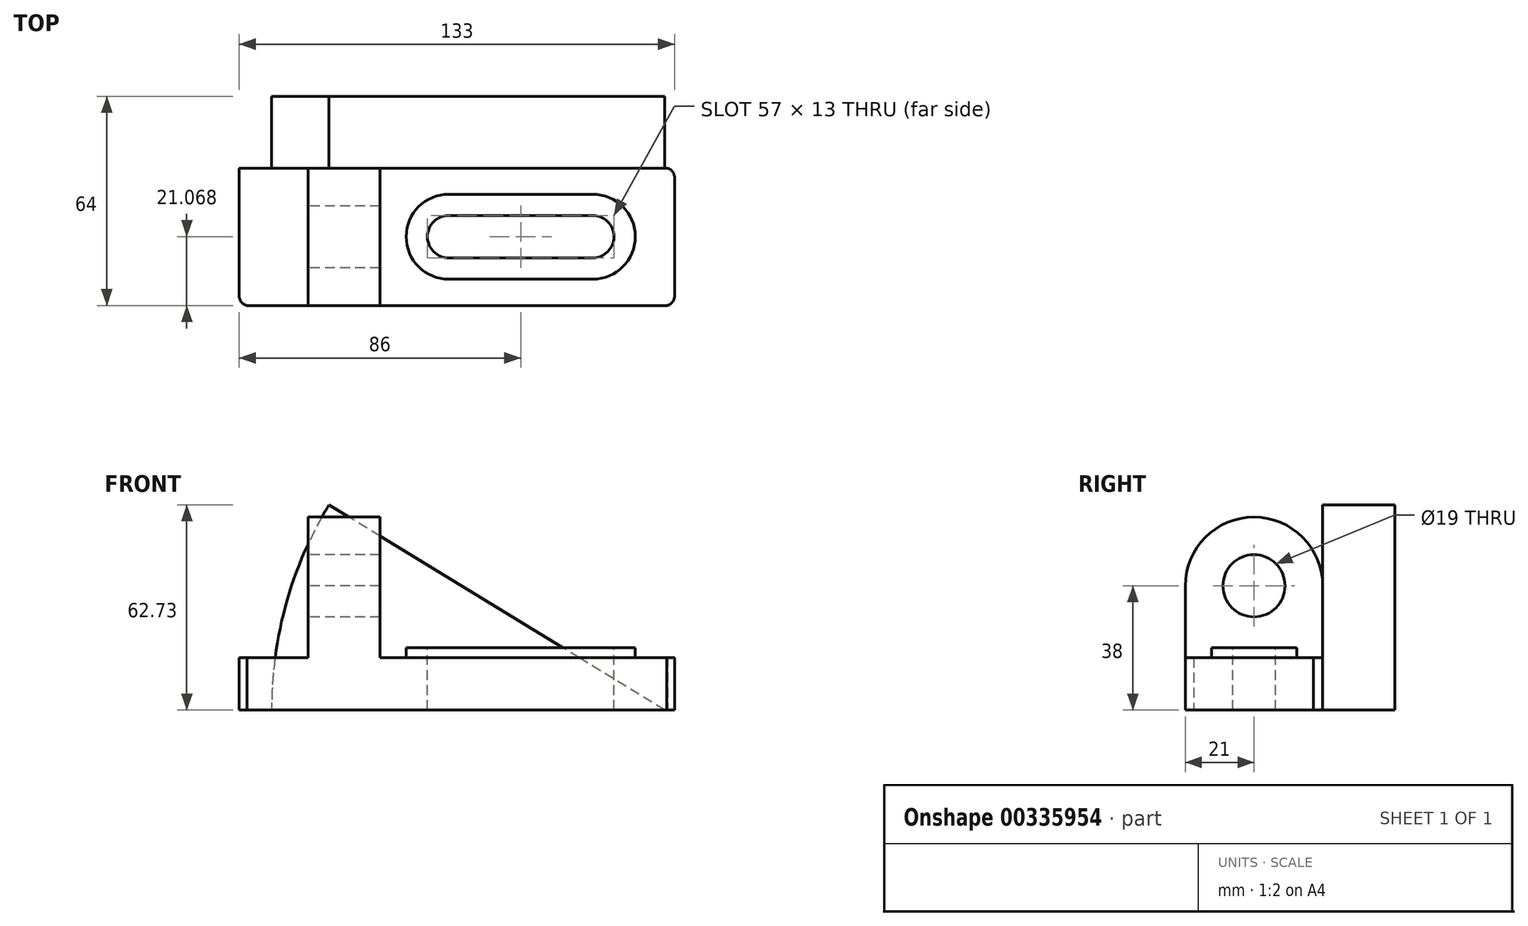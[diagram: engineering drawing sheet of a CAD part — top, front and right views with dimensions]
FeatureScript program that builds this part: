
annotation { "Feature Type Name" : "Feature", "Feature Type Description" : "" }
export const myFeature = defineFeature(function(context is Context, id is Id, definition is map)
    precondition{}
    {
        {
            var Q0;
            Q0=qCreatedBy(makeId("Right.planeOp"),FACE);
            var sketch = newSketch(context, id + "F0", { "sketchPlane" : qUnion([Q0])});
            skLineSegment(sketch, "E0", {"start": v(0, 0) * mm, "end": v(-42, 0) * mm});
            skLineSegment(sketch, "E1", {"start": v(-42, 0) * mm, "end": v(-42, 16) * mm});
            skLineSegment(sketch, "E2", {"start": v(-42, 16) * mm, "end": v(0, 16) * mm});
            skLineSegment(sketch, "E3", {"start": v(0, 16) * mm, "end": v(0, 0) * mm});
            skSolve(sketch);
        }
        {
            var Q0;
            Q0 = qSketchRegion(id + "F0", true);
            extrude(context, id + "F1", {"entities" : qUnion([Q0]), "depth" : 112 * mm});
        }
        {
            var Q0;
            Q0=makeQuery(id+"F1.opExtrude","CAP_FACE",FACE,{"disambiguationData":[OSD([sQuery(id+"F0.wireOp",EDGE,"E0"),sQuery(id+"F0.wireOp",EDGE,"E1"),sQuery(id+"F0.wireOp",EDGE,"E2"),sQuery(id+"F0.wireOp",EDGE,"E3")])],"isStart":true});
            var sketch = newSketch(context, id + "F2", { "sketchPlane" : qUnion([Q0])});
            skLineSegment(sketch, "E4", {"start": v(0, 16) * mm, "end": v(0, 38) * mm});
            skLineSegment(sketch, "E5", {"start": v(0, 38) * mm, "end": v(42, 38) * mm});
            skLineSegment(sketch, "E6", {"start": v(42, 38) * mm, "end": v(42, 16) * mm});
            skLineSegment(sketch, "E7", {"start": v(42, 16) * mm, "end": v(0, 16) * mm});
            skArc(sketch, "E8", {"start": v(42, 38) * mm, "mid": v(21, 59) * mm, "end": v(0, 38) * mm});
            skSolve(sketch);
        }
        {
            var Q0;
            Q0 = qSketchRegion(id + "F2", true);
            extrude(context, id + "F3", {"entities" : qUnion([Q0]), "operationType" : NewBodyOperationType.ADD, "oppositeDirection" : true, "depth" : 22 * mm});
        }
        {
            var Q0;
            Q0=makeQuery(id+"F3.boolean.opBoolean","MERGE",FACE,{"derivedFrom":[makeQuery(id+"F1.opExtrude","CAP_FACE",FACE,{"disambiguationData":[OSD([sQuery(id+"F0.wireOp",EDGE,"E0"),sQuery(id+"F0.wireOp",EDGE,"E1"),sQuery(id+"F0.wireOp",EDGE,"E2"),sQuery(id+"F0.wireOp",EDGE,"E3")])],"isStart":true}),makeQuery(id+"F3.opExtrude","CAP_FACE",FACE,{"disambiguationData":[OSD([sQuery(id+"F2.wireOp",EDGE,"E4"),sQuery(id+"F2.wireOp",EDGE,"E6"),sQuery(id+"F2.wireOp",EDGE,"E7"),sQuery(id+"F2.wireOp",EDGE,"E8")])],"isStart":true})]});
            var sketch = newSketch(context, id + "F4", { "sketchPlane" : qUnion([Q0])});
            skCircle(sketch, "E9", {"center": v(21, 38) * mm, "radius": 9.5 * mm});
            skSolve(sketch);
        }
        {
            var Q0;
            Q0 = qSketchRegion(id + "F4", true);
            extrude(context, id + "F5", {"entities" : qUnion([Q0]), "operationType" : NewBodyOperationType.REMOVE, "oppositeDirection" : true, "depth" : 25 * mm});
        }
        {
            var Q0;
            Q0=makeQuery(id+"F3.boolean.opBoolean","MERGE",FACE,{"derivedFrom":[makeQuery(id+"F1.opExtrude","CAP_FACE",FACE,{"disambiguationData":[OSD([sQuery(id+"F0.wireOp",EDGE,"E0"),sQuery(id+"F0.wireOp",EDGE,"E1"),sQuery(id+"F0.wireOp",EDGE,"E2"),sQuery(id+"F0.wireOp",EDGE,"E3")])],"isStart":true}),makeQuery(id+"F3.opExtrude","CAP_FACE",FACE,{"disambiguationData":[OSD([sQuery(id+"F2.wireOp",EDGE,"E4"),sQuery(id+"F2.wireOp",EDGE,"E6"),sQuery(id+"F2.wireOp",EDGE,"E7"),sQuery(id+"F2.wireOp",EDGE,"E8")])],"isStart":true})]});
            var sketch = newSketch(context, id + "F6", { "sketchPlane" : qUnion([Q0])});
            skLineSegment(sketch, "E10", {"start": v(0, 0) * mm, "end": v(42, 0) * mm});
            skLineSegment(sketch, "E11", {"start": v(42, 0) * mm, "end": v(42, 16) * mm});
            skLineSegment(sketch, "E12", {"start": v(42, 16) * mm, "end": v(0, 16) * mm});
            skLineSegment(sketch, "E13", {"start": v(0, 16) * mm, "end": v(0, 0) * mm});
            skSolve(sketch);
        }
        {
            var Q0;
            Q0 = qSketchRegion(id + "F6", true);
            extrude(context, id + "F7", {"entities" : qUnion([Q0]), "operationType" : NewBodyOperationType.ADD, "depth" : 21 * mm});
        }
        {
            var Q0;
            Q0=makeQuery(id+"F1.opExtrude","SWEPT_FACE",FACE,{"disambiguationData":[OSD([sQuery(id+"F0.wireOp",EDGE,"E2")])]});
            var sketch = newSketch(context, id + "F8", { "sketchPlane" : qUnion([Q0])});
            skLineSegment(sketch, "E14", {"start": v(0, 0) * mm, "end": v(-21, 0) * mm, "construction": true});
            skLineSegment(sketch, "E15", {"start": v(0, 0) * mm, "end": v(22, 0) * mm, "construction": true});
            skLineSegment(sketch, "E16", {"start": v(22, 0) * mm, "end": v(43, 0) * mm, "construction": true});
            skLineSegment(sketch, "E17", {"start": v(43, 0) * mm, "end": v(87, 0) * mm, "construction": true});
            skLineSegment(sketch, "E18", {"start": v(43, -20.93) * mm, "end": v(43, -21) * mm});
            skArc(sketch, "E19", {"start": v(43, -7.93) * mm, "mid": v(30, -20.93) * mm, "end": v(43, -33.93) * mm});
            skArc(sketch, "E20", {"start": v(87, -33.93) * mm, "mid": v(100, -20.93) * mm, "end": v(87, -7.93) * mm});
            skLineSegment(sketch, "E21", {"start": v(43, -7.93) * mm, "end": v(87, -7.93) * mm});
            skLineSegment(sketch, "E22", {"start": v(43, -33.93) * mm, "end": v(87, -33.93) * mm});
            skSolve(sketch);
        }
        {
            var Q0;
            Q0 = qSketchRegion(id + "F8", true);
            extrude(context, id + "F9", {"entities" : qUnion([Q0]), "operationType" : NewBodyOperationType.ADD, "depth" : 3 * mm});
        }
        {
            var Q0;
            Q0=makeQuery(id+"F9.opExtrude","CAP_FACE",FACE,{"disambiguationData":[OSD([sQuery(id+"F8.wireOp",EDGE,"E19"),sQuery(id+"F8.wireOp",EDGE,"E20"),sQuery(id+"F8.wireOp",EDGE,"E21"),sQuery(id+"F8.wireOp",EDGE,"E22")])],"isStart":false});
            var sketch = newSketch(context, id + "F10", { "sketchPlane" : qUnion([Q0])});
            skLineSegment(sketch, "E23", {"start": v(43, -7.93) * mm, "end": v(43, -14.43) * mm, "construction": true});
            skLineSegment(sketch, "E24", {"start": v(43, -33.93) * mm, "end": v(43, -27.43) * mm, "construction": true});
            skLineSegment(sketch, "E25", {"start": v(87, -33.93) * mm, "end": v(87, -27.43) * mm, "construction": true});
            skLineSegment(sketch, "E26", {"start": v(87, -7.93) * mm, "end": v(87, -14.43) * mm, "construction": true});
            skArc(sketch, "E27", {"start": v(43, -14.43) * mm, "mid": v(36.5, -20.93) * mm, "end": v(43, -27.43) * mm});
            skArc(sketch, "E28", {"start": v(87, -27.43) * mm, "mid": v(93.5, -20.93) * mm, "end": v(87, -14.43) * mm});
            skLineSegment(sketch, "E29", {"start": v(43, -14.43) * mm, "end": v(87, -14.43) * mm});
            skLineSegment(sketch, "E30", {"start": v(87, -27.43) * mm, "end": v(43, -27.43) * mm});
            skSolve(sketch);
        }
        {
            var Q0;
            Q0 = qSketchRegion(id + "F10", true);
            extrude(context, id + "F11", {"entities" : qUnion([Q0]), "operationType" : NewBodyOperationType.REMOVE, "oppositeDirection" : true, "depth" : 58 * mm});
        }
        {
            var Q0;
            Q0=qCreatedBy(makeId("Top.planeOp"),FACE);
            var sketch = newSketch(context, id + "F12", { "sketchPlane" : qUnion([Q0])});
            skLineSegment(sketch, "E31", {"start": v(0, 0) * mm, "end": v(-21, 0) * mm});
            skLineSegment(sketch, "E32", {"start": v(0, 0) * mm, "end": v(-21, 0) * mm, "construction": true});
            skArc(sketch, "E33", {"start": v(-17.6, 0) * mm, "mid": v(-19.91, -0.66) * mm, "end": v(-21, -2.8) * mm});
            skArc(sketch, "E34", {"start": v(-21, -38.64) * mm, "mid": v(-20.49, -40.79) * mm, "end": v(-18.65, -42) * mm});
            skArc(sketch, "E35", {"start": v(112, -2.8) * mm, "mid": v(110.76, -0.44) * mm, "end": v(108.14, 0) * mm});
            skArc(sketch, "E36", {"start": v(109.62, -42) * mm, "mid": v(111.33, -40.95) * mm, "end": v(112, -39.06) * mm});
            skPoint(sketch, "E36.endSnap0", {"position": v(112, -21) * mm});
            skLineSegment(sketch, "E37", {"start": v(-17.6, 0) * mm, "end": v(-21, 0) * mm});
            skLineSegment(sketch, "E38", {"start": v(-18.65, -42) * mm, "end": v(-21.89, -42) * mm});
            skLineSegment(sketch, "E39", {"start": v(-21, -38.64) * mm, "end": v(-21, -43.33) * mm});
            skLineSegment(sketch, "E40", {"start": v(109.62, -42) * mm, "end": v(122.13, -42) * mm});
            skLineSegment(sketch, "E41", {"start": v(112, -39.06) * mm, "end": v(112, -47.39) * mm});
            skLineSegment(sketch, "E42", {"start": v(112, -2.8) * mm, "end": v(112, 6.3) * mm});
            skLineSegment(sketch, "E43", {"start": v(108.14, 0) * mm, "end": v(119.51, 0) * mm});
            skSolve(sketch);
        }
        {
            var Q0;
            Q0 = qSketchRegion(id + "F12", true);
            extrude(context, id + "F13", {"entities" : qUnion([Q0]), "operationType" : NewBodyOperationType.REMOVE, "depth" : 54 * mm});
        }
        {
            var Q0;
            Q0=makeQuery(id+"F7.boolean.opBoolean","MERGE",FACE,{"derivedFrom":[makeQuery(id+"F3.boolean.opBoolean","MERGE",FACE,{"derivedFrom":[makeQuery(id+"F1.opExtrude","SWEPT_FACE",FACE,{"disambiguationData":[OSD([sQuery(id+"F0.wireOp",EDGE,"E3")])]}),makeQuery(id+"F3.opExtrude","SWEPT_FACE",FACE,{"disambiguationData":[OSD([sQuery(id+"F2.wireOp",EDGE,"E4")])]})]}),makeQuery(id+"F7.opExtrude","SWEPT_FACE",FACE,{"disambiguationData":[OSD([sQuery(id+"F6.wireOp",EDGE,"E13")])]})]});
            var sketch = newSketch(context, id + "F14", { "sketchPlane" : qUnion([Q0])});
            skLineSegment(sketch, "E44", {"start": v(-109.86, 0) * mm, "end": v(-109, 0) * mm});
            skArc(sketch, "E45", {"start": v(11.14, 0) * mm, "mid": v(6.67, 32.57) * mm, "end": v(-6.4, 62.73) * mm});
            skLineSegment(sketch, "E46", {"start": v(-109.86, 0) * mm, "end": v(11.14, 0) * mm});
            skLineSegment(sketch, "E47", {"start": v(-109, 0) * mm, "end": v(-6.4, 62.73) * mm});
            skSolve(sketch);
        }
        {
            var Q0;
            Q0 = qSketchRegion(id + "F14", true);
            extrude(context, id + "F15", {"entities" : qUnion([Q0]), "operationType" : NewBodyOperationType.ADD, "depth" : 22 * mm});
        }
    });
